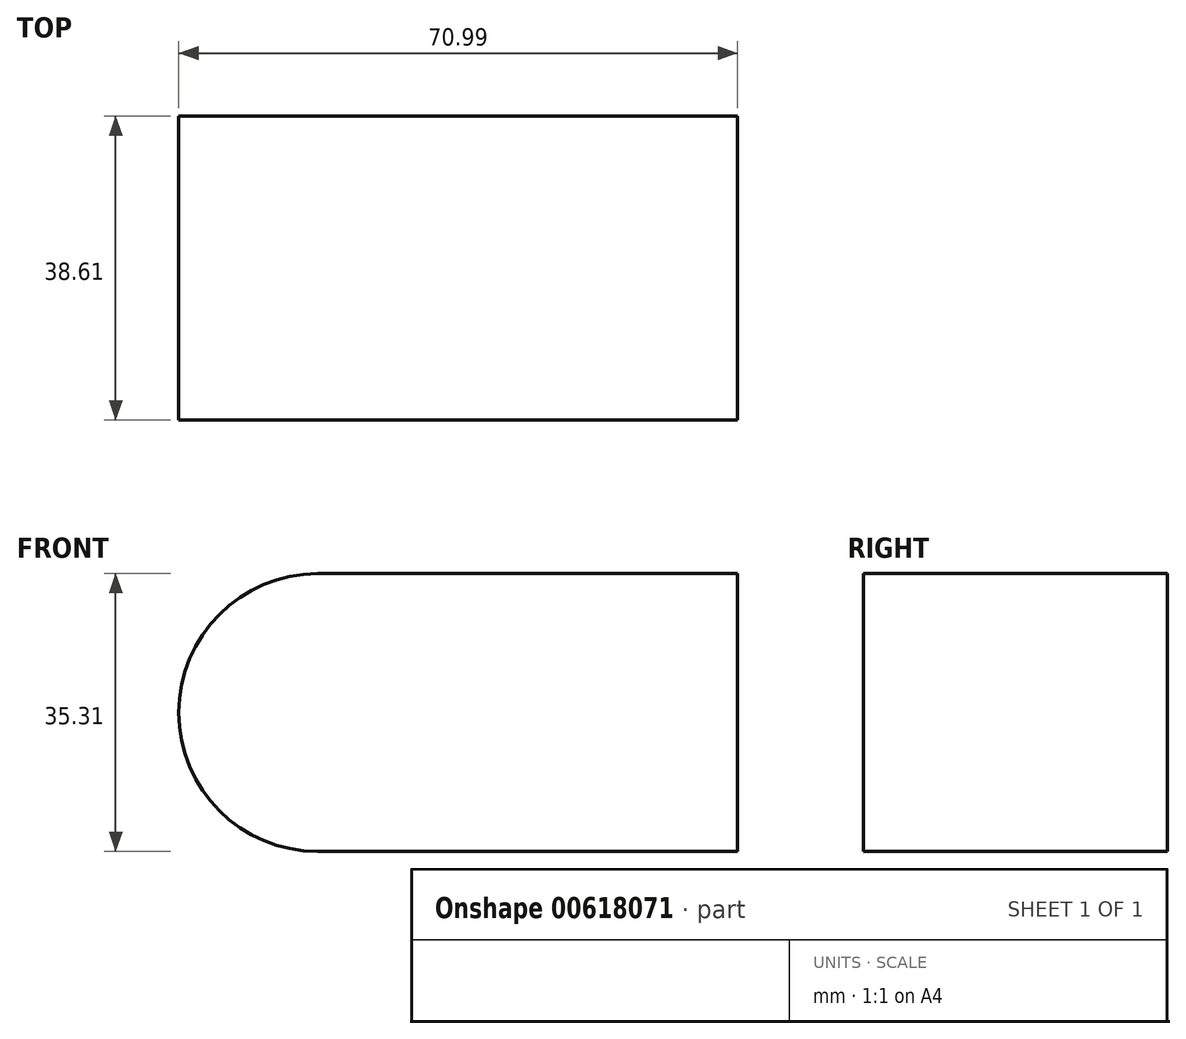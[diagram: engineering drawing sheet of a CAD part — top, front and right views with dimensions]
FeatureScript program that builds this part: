
annotation { "Feature Type Name" : "Feature", "Feature Type Description" : "" }
export const myFeature = defineFeature(function(context is Context, id is Id, definition is map)
    precondition{}
    {
        {
            var Q0;
            Q0=qCreatedBy(makeId("Front.planeOp"),FACE);
            var sketch = newSketch(context, id + "F0", { "sketchPlane" : qUnion([Q0])});
            skLineSegment(sketch, "E0", {"start": v(0, 0) * mm, "end": v(0, 35.3) * mm});
            skLineSegment(sketch, "E1", {"start": v(0, 35.3) * mm, "end": v(53.34, 35.3) * mm});
            skLineSegment(sketch, "E2", {"start": v(53.34, 35.3) * mm, "end": v(53.34, 0) * mm});
            skLineSegment(sketch, "E3", {"start": v(0, 0) * mm, "end": v(53.34, 0) * mm});
            skArc(sketch, "E4", {"start": v(0, 35.3) * mm, "mid": v(-17.65, 17.65) * mm, "end": v(0, 0) * mm});
            skSolve(sketch);
        }
        {
            var Q0;
            Q0 = qSketchRegion(id + "F0", true);
            extrude(context, id + "F1", {"entities" : qUnion([Q0]), "depth" : 38.6 * mm, "offsetDistance" : 25.4 * mm});
        }
    });
